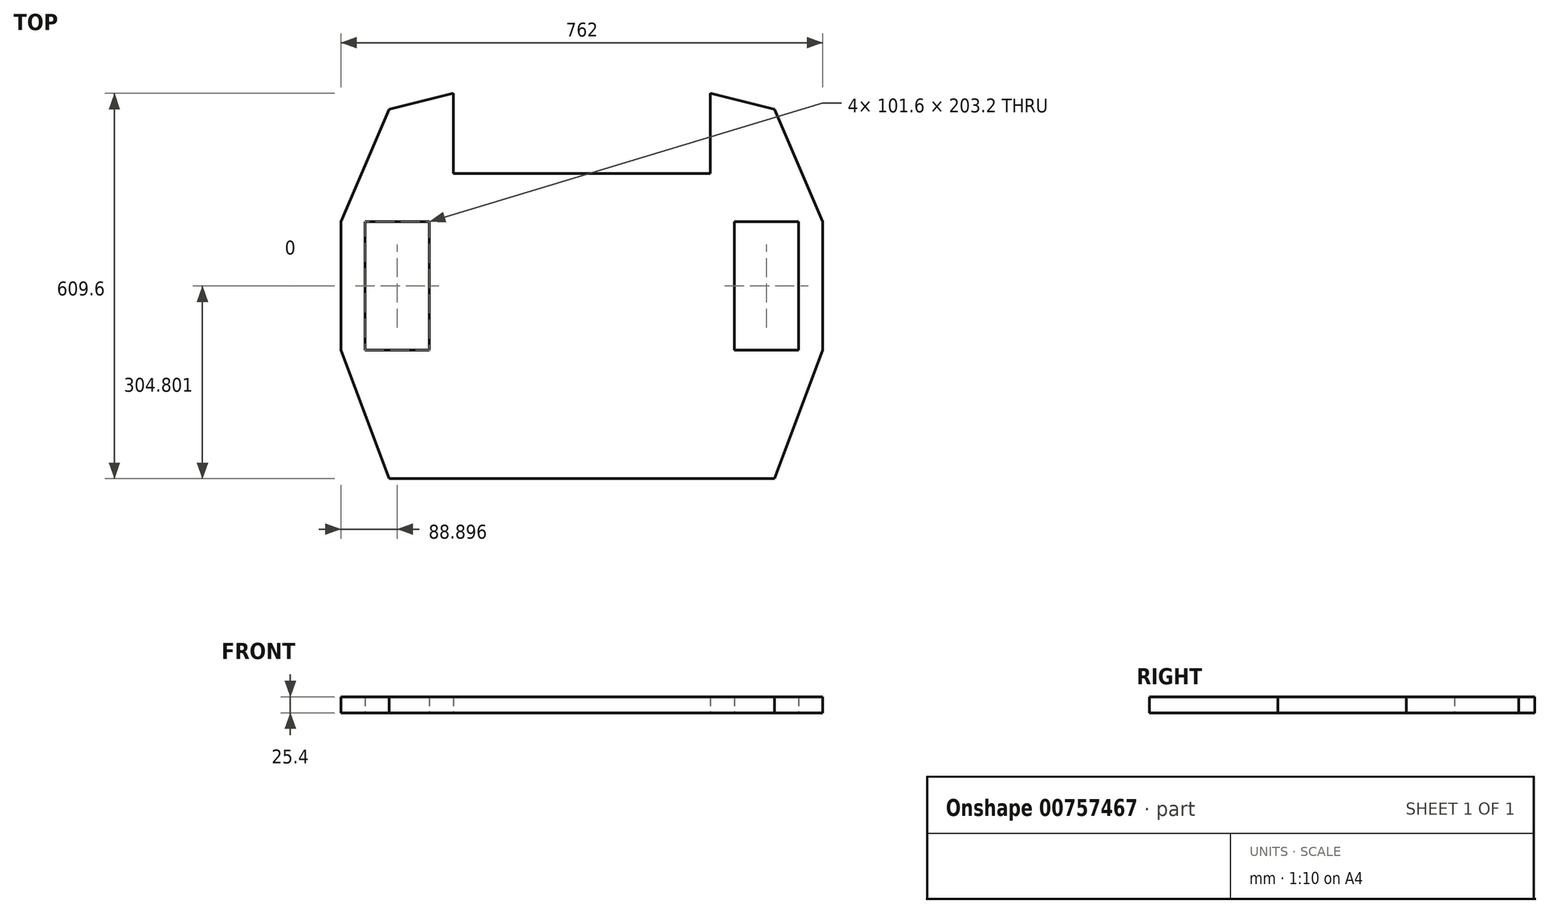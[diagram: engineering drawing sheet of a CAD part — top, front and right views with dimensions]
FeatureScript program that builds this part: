
annotation { "Feature Type Name" : "Feature", "Feature Type Description" : "" }
export const myFeature = defineFeature(function(context is Context, id is Id, definition is map)
    precondition{}
    {
        {
            var Q0;
            Q0=qCreatedBy(makeId("Top.planeOp"),FACE);
            var sketch = newSketch(context, id + "F0", { "sketchPlane" : qUnion([Q0])});
            skLineSegment(sketch, "E0", {"start": v(-321.42, 342.04) * mm, "end": v(-397.62, 164.24) * mm});
            skLineSegment(sketch, "E1", {"start": v(-397.62, 164.24) * mm, "end": v(-397.62, -38.96) * mm});
            skLineSegment(sketch, "E2", {"start": v(-397.62, -38.96) * mm, "end": v(-321.42, -242.16) * mm});
            skLineSegment(sketch, "E3", {"start": v(-321.42, -242.16) * mm, "end": v(288.18, -242.16) * mm});
            skLineSegment(sketch, "E4", {"start": v(288.18, -242.16) * mm, "end": v(364.38, -38.96) * mm});
            skLineSegment(sketch, "E5", {"start": v(364.38, -38.96) * mm, "end": v(364.38, 164.24) * mm});
            skLineSegment(sketch, "E6", {"start": v(364.38, 164.24) * mm, "end": v(288.18, 342.04) * mm});
            skLineSegment(sketch, "E7", {"start": v(-321.42, 342.04) * mm, "end": v(-219.82, 367.44) * mm});
            skLineSegment(sketch, "E8", {"start": v(-219.82, 367.44) * mm, "end": v(-219.82, 240.44) * mm});
            skLineSegment(sketch, "E9", {"start": v(-219.82, 240.44) * mm, "end": v(186.58, 240.44) * mm});
            skLineSegment(sketch, "E10", {"start": v(186.58, 240.44) * mm, "end": v(186.58, 367.44) * mm});
            skLineSegment(sketch, "E11", {"start": v(186.58, 367.44) * mm, "end": v(288.18, 342.04) * mm});
            skLineSegment(sketch, "E12.bottom", {"start": v(-359.52, 164.24) * mm, "end": v(-257.92, 164.24) * mm});
            skLineSegment(sketch, "E12.top", {"start": v(-359.52, -38.96) * mm, "end": v(-257.92, -38.96) * mm});
            skLineSegment(sketch, "E12.left", {"start": v(-359.52, 164.24) * mm, "end": v(-359.52, -38.96) * mm});
            skLineSegment(sketch, "E12.right", {"start": v(-257.92, 164.24) * mm, "end": v(-257.92, -38.96) * mm});
            skLineSegment(sketch, "E13.bottom", {"start": v(326.28, 164.24) * mm, "end": v(224.68, 164.24) * mm});
            skLineSegment(sketch, "E13.top", {"start": v(326.28, -38.96) * mm, "end": v(224.68, -38.96) * mm});
            skLineSegment(sketch, "E13.left", {"start": v(326.28, 164.24) * mm, "end": v(326.28, -38.96) * mm});
            skLineSegment(sketch, "E13.right", {"start": v(224.68, 164.24) * mm, "end": v(224.68, -38.96) * mm});
            skSolve(sketch);
        }
        {
            var Q0;
            Q0=makeQuery(id+"F0.imprint","IMPRINT",FACE,{"disambiguationData":[TD([[makeQuery(id+"F0.imprint","IMPRINT",EDGE,{"derivedFrom":sQuery(id+"F0.wireOp",EDGE,"E0")}),1.0]])]});
            extrude(context, id + "F1", {"entities" : qUnion([Q0]), "depth" : 25.4 * mm, "offsetDistance" : 25.4 * mm});
        }
    });
